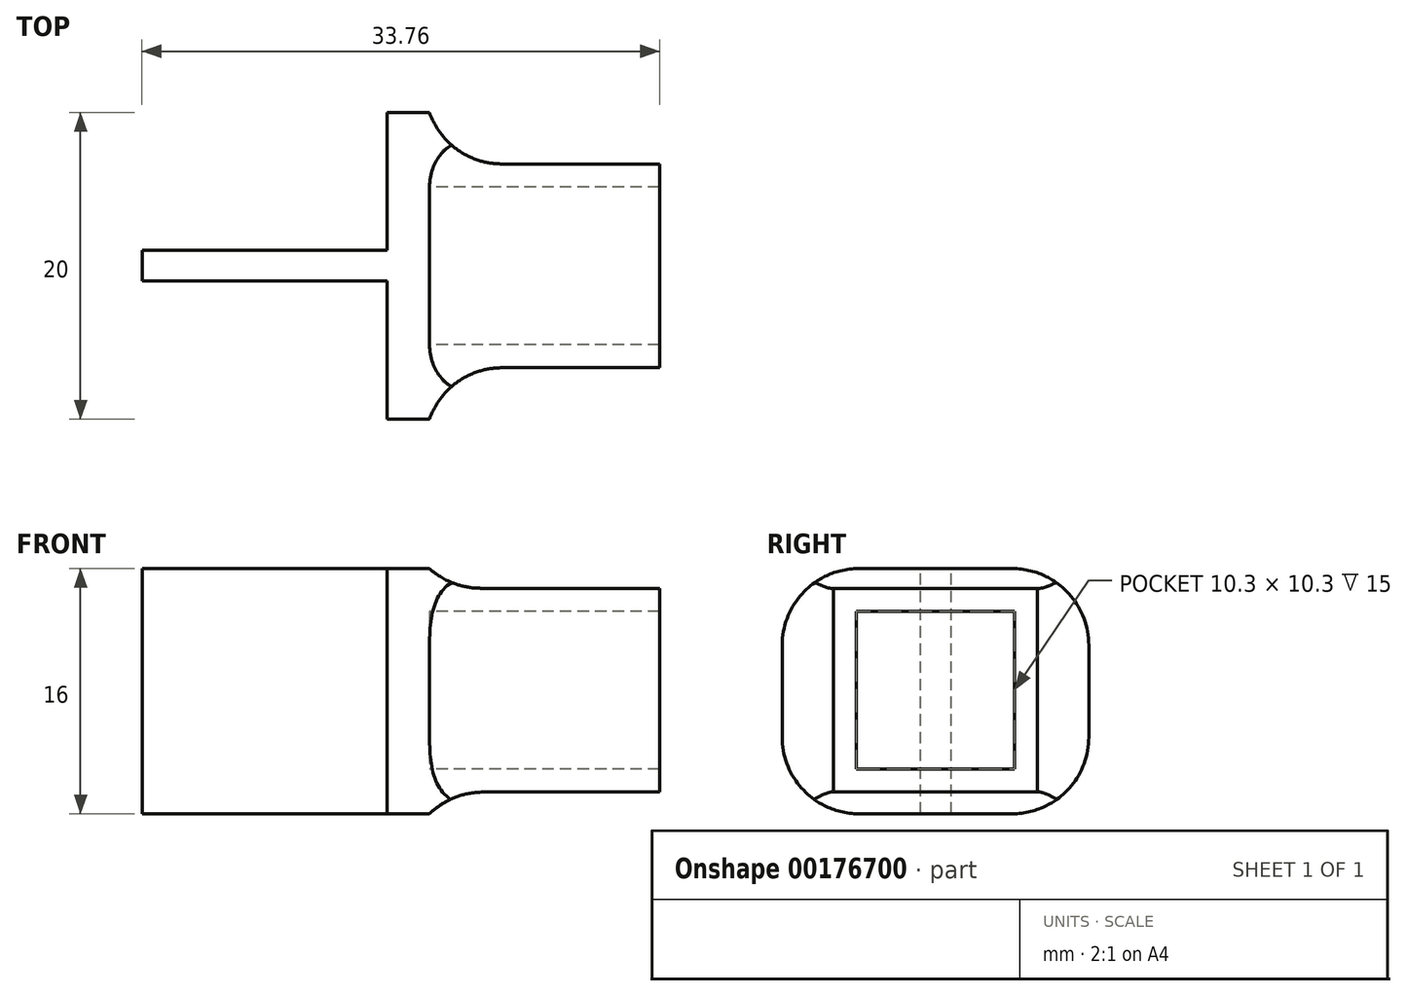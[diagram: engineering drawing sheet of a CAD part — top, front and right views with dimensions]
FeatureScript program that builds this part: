
annotation { "Feature Type Name" : "Feature", "Feature Type Description" : "" }
export const myFeature = defineFeature(function(context is Context, id is Id, definition is map)
    precondition{}
    {
        {
            var Q0;
            Q0=qCreatedBy(makeId("Top.planeOp"),FACE);
            var sketch = newSketch(context, id + "F0", { "sketchPlane" : qUnion([Q0])});
            skLineSegment(sketch, "E0.bottom", {"start": v(-1.37, 10) * mm, "end": v(1.38, 10) * mm});
            skLineSegment(sketch, "E0.top", {"start": v(-1.38, -10) * mm, "end": v(1.37, -10) * mm});
            skLineSegment(sketch, "E0.left", {"start": v(-1.37, 10) * mm, "end": v(-1.38, -10) * mm});
            skLineSegment(sketch, "E0.right", {"start": v(1.38, 10) * mm, "end": v(1.37, -10) * mm});
            skPoint(sketch, "E0.middle", {"position": v(0, 0) * mm});
            skSolve(sketch);
        }
        {
            var Q0;
            Q0=qSketchRegion(id+"F0",true);
            extrude(context, id + "F1", {"entities" : qUnion([Q0]), "depth" : 16 * mm});
        }
        {
            var Q0;
            Q0=makeQuery(id+"F1.opExtrude","SWEPT_FACE",FACE,{"disambiguationData":[OSD([sQuery(id+"F0.wireOp",EDGE,"E0.right")])]});
            var sketch = newSketch(context, id + "F2", { "sketchPlane" : qUnion([Q0])});
            skLineSegment(sketch, "E1.bottom", {"start": v(-10, 16) * mm, "end": v(10, 16) * mm});
            skLineSegment(sketch, "E1.top", {"start": v(-10, 0) * mm, "end": v(10, 0) * mm});
            skLineSegment(sketch, "E1.left", {"start": v(-10, 16) * mm, "end": v(-10, 0) * mm});
            skLineSegment(sketch, "E1.right", {"start": v(10, 16) * mm, "end": v(10, 0) * mm});
            skLineSegment(sketch, "E2.bottom", {"start": v(-5.15, 13.22) * mm, "end": v(5.15, 13.22) * mm});
            skLineSegment(sketch, "E2.top", {"start": v(-5.15, 2.92) * mm, "end": v(5.15, 2.92) * mm});
            skLineSegment(sketch, "E2.left", {"start": v(-5.15, 13.22) * mm, "end": v(-5.15, 2.92) * mm});
            skLineSegment(sketch, "E2.right", {"start": v(5.15, 13.22) * mm, "end": v(5.15, 2.92) * mm});
            skLineSegment(sketch, "E3.0", {"start": v(-6.65, 14.72) * mm, "end": v(6.65, 14.72) * mm});
            skLineSegment(sketch, "E3.1", {"start": v(-6.65, 14.72) * mm, "end": v(-6.65, 1.42) * mm});
            skLineSegment(sketch, "E3.2", {"start": v(-6.65, 1.42) * mm, "end": v(6.65, 1.42) * mm});
            skLineSegment(sketch, "E3.3", {"start": v(6.65, 14.72) * mm, "end": v(6.65, 1.42) * mm});
            skLineSegment(sketch, "E4", {"start": v(0, 0) * mm, "end": v(0, 16) * mm});
            skPoint(sketch, "E5", {"position": v(0, 8) * mm});
            skPoint(sketch, "E6.positionSnap0", {"position": v(0, 13.22) * mm});
            skPoint(sketch, "E7.positionSnap0", {"position": v(0, 16) * mm});
            skPoint(sketch, "E7.positionSnap1", {"position": v(10, 8) * mm});
            skSolve(sketch);
        }
        {
            var Q0;
            Q0=qSketchRegion(id+"F2",true);
            var Q1;
            Q1=makeQuery(id+"F2.imprint","IMPRINT",FACE,{"disambiguationData":[TD([[makeQuery(id+"F2.imprint","IMPRINT",EDGE,{"derivedFrom":sQuery(id+"F2.wireOp",EDGE,"E2.bottom")}),-1.0]])]});
            var Q2;
            Q2=makeQuery(id+"F2.imprint","IMPRINT",FACE,{"disambiguationData":[TD([[makeQuery(id+"F2.imprint","IMPRINT",EDGE,{"derivedFrom":sQuery(id+"F2.wireOp",EDGE,"E2.bottom")}),1.0]])]});
            var Q3;
            Q3=makeQuery(id+"F2.imprint","IMPRINT",FACE,{"disambiguationData":[TD([[makeQuery(id+"F2.imprint","IMPRINT",EDGE,{"derivedFrom":sQuery(id+"F2.wireOp",EDGE,"4b76e74c-1ac9-4312-af6a-232a9c3240f70.MirrorCS")}),-1.0]])]});
            var Q4;
            Q4=makeQuery(id+"F2.imprint","IMPRINT",FACE,{"disambiguationData":[TD([[makeQuery(id+"F2.imprint","IMPRINT",EDGE,{"derivedFrom":sQuery(id+"F2.wireOp",EDGE,"4b76e74c-1ac9-4312-af6a-232a9c3240f70.MirrorCS")}),1.0]])]});
            extrude(context, id + "F3", {"entities" : qUnion([Q0, Q1, Q2, Q3, Q4]), "operationType" : NewBodyOperationType.ADD, "oppositeDirection" : true, "depth" : 2.75 * mm});
        }
        {
            var Q0;
            Q0=makeQuery(id+"F2.imprint","IMPRINT",FACE,{"disambiguationData":[TD([[makeQuery(id+"F2.imprint","IMPRINT",EDGE,{"derivedFrom":sQuery(id+"F2.wireOp",EDGE,"E2.bottom")}),1.0]])]});
            var Q1;
            Q1=makeQuery(id+"F2.imprint","IMPRINT",FACE,{"disambiguationData":[TD([[makeQuery(id+"F2.imprint","IMPRINT",EDGE,{"derivedFrom":sQuery(id+"F2.wireOp",EDGE,"4b76e74c-1ac9-4312-af6a-232a9c3240f70.MirrorCS")}),-1.0]])]});
            extrude(context, id + "F4", {"entities" : qUnion([Q0, Q1]), "operationType" : NewBodyOperationType.ADD, "depth" : 15 * mm});
        }
        {
            var Q0;
            Q0=makeQuery(id+"F3.boolean.opBoolean","INTERSECT",EDGE,{"derivedFrom":[makeQuery(id+"F1.opExtrude","SWEPT_FACE",FACE,{"disambiguationData":[OSD([sQuery(id+"F0.wireOp",EDGE,"E0.bottom")])]}),makeQuery(id+"F3.opExtrude","CAP_FACE",FACE,{"disambiguationData":[OSD([sQuery(id+"F2.wireOp",EDGE,"E1.bottom"),sQuery(id+"F2.wireOp",EDGE,"E1.top"),sQuery(id+"F2.wireOp",EDGE,"E1.left"),sQuery(id+"F2.wireOp",EDGE,"E1.right")])],"isStart":false})]});
            var Q1;
            Q1=makeQuery(id+"F3.boolean.opBoolean","INTERSECT",EDGE,{"derivedFrom":[makeQuery(id+"F1.opExtrude","SWEPT_FACE",FACE,{"disambiguationData":[OSD([sQuery(id+"F0.wireOp",EDGE,"E0.top")])]}),makeQuery(id+"F3.opExtrude","CAP_FACE",FACE,{"disambiguationData":[OSD([sQuery(id+"F2.wireOp",EDGE,"E1.bottom"),sQuery(id+"F2.wireOp",EDGE,"E1.top"),sQuery(id+"F2.wireOp",EDGE,"E1.left"),sQuery(id+"F2.wireOp",EDGE,"E1.right")])],"isStart":false})]});
            var Q2;
            Q2=makeQuery(id+"F4.opExtrude","CAP_EDGE",EDGE,{"disambiguationData":[OSD([sQuery(id+"F2.wireOp",EDGE,"E3.0")])],"isStart":true});
            var Q3;
            Q3=makeQuery(id+"F4.opExtrude","CAP_EDGE",EDGE,{"disambiguationData":[OSD([sQuery(id+"F2.wireOp",EDGE,"E3.1")])],"isStart":true});
            var Q4;
            Q4=makeQuery(id+"F4.opExtrude","CAP_EDGE",EDGE,{"disambiguationData":[OSD([sQuery(id+"F2.wireOp",EDGE,"E3.3")])],"isStart":true});
            var Q5;
            Q5=makeQuery(id+"F4.opExtrude","CAP_EDGE",EDGE,{"disambiguationData":[OSD([sQuery(id+"F2.wireOp",EDGE,"E3.2")])],"isStart":true});
            fillet(context, id + "F5", {"entities" : qUnion([Q0, Q1, Q2, Q3, Q4, Q5]), "radius" : 5 * mm, "tangentPropagation" : true, "allowEdgeOverflow" : false});
        }
        {
            var Q0;
            Q0=makeQuery(id+"F1.opExtrude","CAP_EDGE",EDGE,{"disambiguationData":[OSD([sQuery(id+"F0.wireOp",EDGE,"E0.top")])],"isStart":true});
            var Q1;
            Q1=makeQuery(id+"F1.opExtrude","CAP_EDGE",EDGE,{"disambiguationData":[OSD([sQuery(id+"F0.wireOp",EDGE,"E0.top")])],"isStart":false});
            var Q2;
            Q2=makeQuery(id+"F1.opExtrude","CAP_EDGE",EDGE,{"disambiguationData":[OSD([sQuery(id+"F0.wireOp",EDGE,"E0.bottom")])],"isStart":false});
            var Q3;
            Q3=makeQuery(id+"F1.opExtrude","CAP_EDGE",EDGE,{"disambiguationData":[OSD([sQuery(id+"F0.wireOp",EDGE,"E0.bottom")])],"isStart":true});
            fillet(context, id + "F6", {"entities" : qUnion([Q0, Q1, Q2, Q3]), "radius" : 5 * mm, "tangentPropagation" : true, "allowEdgeOverflow" : false});
        }
        {
            var Q0;
            Q0=makeQuery(id+"F1.opExtrude","SWEPT_FACE",FACE,{"disambiguationData":[OSD([sQuery(id+"F0.wireOp",EDGE,"E0.left")])]});
            var sketch = newSketch(context, id + "F7", { "sketchPlane" : qUnion([Q0])});
            skLineSegment(sketch, "E8.bottom", {"start": v(-1.01, 0) * mm, "end": v(0.99, 0) * mm});
            skLineSegment(sketch, "E8.top", {"start": v(-1.01, 16) * mm, "end": v(0.99, 16) * mm});
            skLineSegment(sketch, "E8.left", {"start": v(-1.01, 0) * mm, "end": v(-1.01, 16) * mm});
            skLineSegment(sketch, "E8.right", {"start": v(0.99, 0) * mm, "end": v(0.99, 16) * mm});
            skSolve(sketch);
        }
        {
            var Q0;
            Q0 = qSketchRegion(id + "F7", true);
            extrude(context, id + "F8", {"entities" : qUnion([Q0]), "operationType" : NewBodyOperationType.ADD, "depth" : 16 * mm});
        }
    });
